# Revit family: 07611_DAO-V_1R
name_source: partatom
category: Air Terminals
revit_build: Autodesk Revit MEP 2012 (Build: 20110309_2315(x64)
units: mm (PartAtom-declared; Revit-internal decimal feet)

## types (5) — shared parameters
Description = Difusor Lineal Oculto
Función = Inyección
Longitud Mín-Máx. = 24" (0.6096 mts)  a 141 3/4" (3.60 mts)
Manufacturer = INNES
Material = Aluminio y acero
Model = DAO-V-1R
Nota1 = .
Nota2 = .
Posición de Instalación = Muro/Techo
Tipo de Cuello = Rectangular
Type Comments = Descarga Vertical con 1 Ranura
URL = https://www.innes.com.mx
Visible_Texto = No
Visible_Texto2 = No

## per-type parameters (varying)
| type | Conect_Ancho | Conect_Largo | Largo_Requerido | Separacion_Requerida | Var1 | Var_Sepa |
| Separación 1" | 2.65 " | 48 " | 48 " | 1 " | 24 " | 1 " |
| Separación 1.5" | 3.15 " | 60 " | 60 " | 1.5 " | 30 " | 1.5 " |
| Separación 2" | 3.65 " | 72 " | 72 " | 2 " | 36 " | 2 " |
| Separación 2.5" | 4.15 " | 96 " | 96 " | 2.5 " | 48 " | 2.5 " |
| Separación 3" | 4.65 " | 118 " | 118 " | 3 " | 59 " | 3 " |

## geometry (parser evidence)
native form markers: Sweep x10
no freeform markers — native parametric forms only
